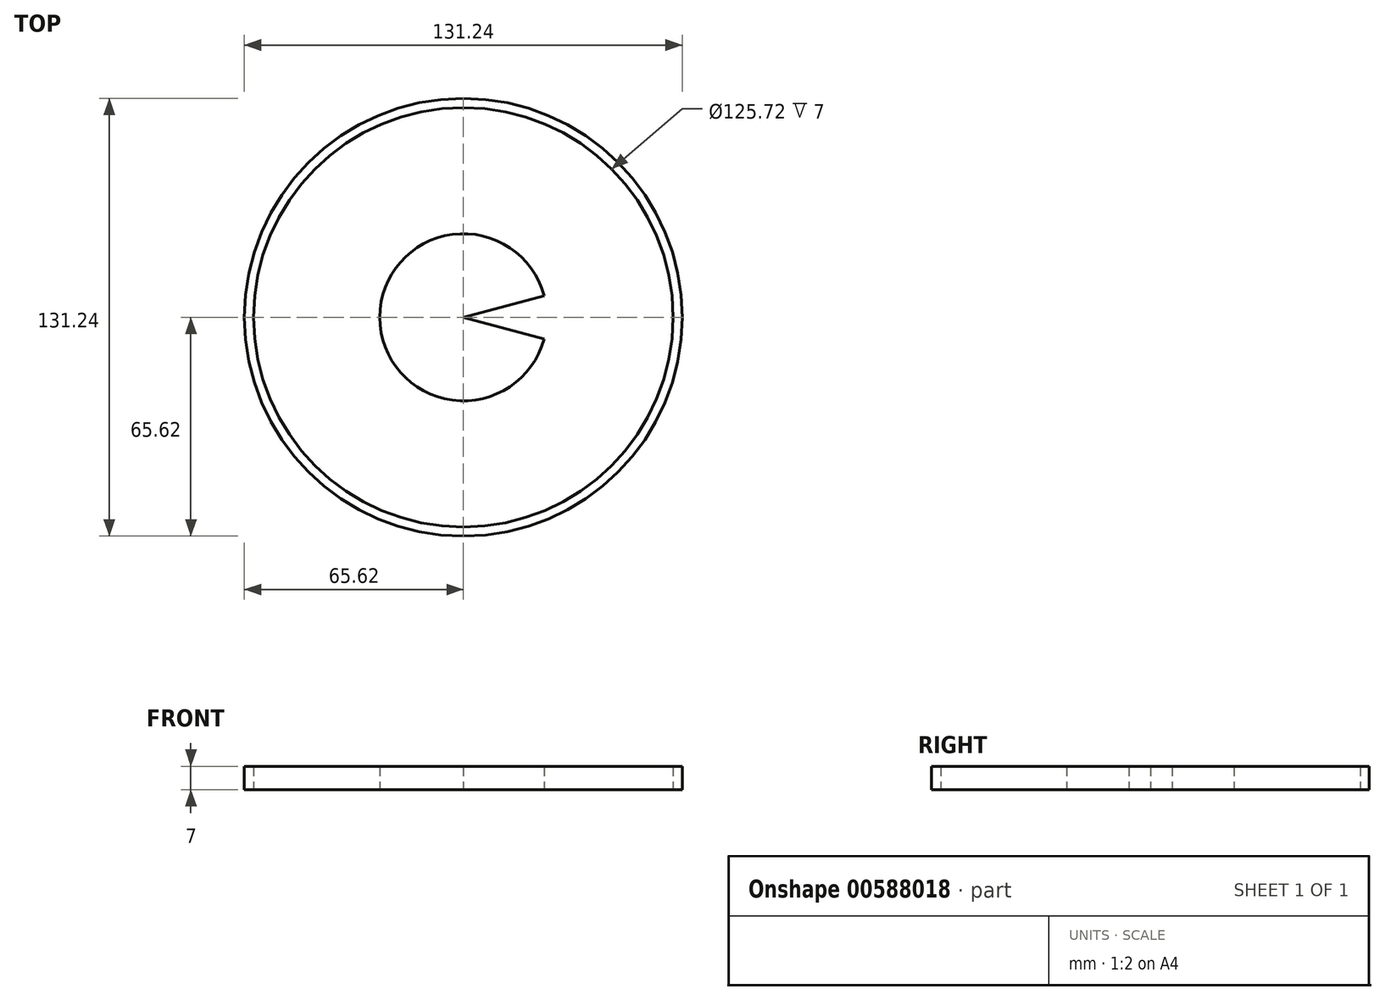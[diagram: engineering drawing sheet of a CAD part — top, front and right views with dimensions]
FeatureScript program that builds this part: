
annotation { "Feature Type Name" : "Feature", "Feature Type Description" : "" }
export const myFeature = defineFeature(function(context is Context, id is Id, definition is map)
    precondition{}
    {
        {
            var Q0;
            Q0=qCreatedBy(makeId("Top.planeOp"),FACE);
            var sketch = newSketch(context, id + "F0", { "sketchPlane" : qUnion([Q0])});
            skCircle(sketch, "E0", {"center": v(0, 0) * mm, "radius": 65.62 * mm});
            skCircle(sketch, "E1", {"center": v(0, 0) * mm, "radius": 62.86 * mm});
            skCircle(sketch, "E2.cCircle", {"center": v(0, 0) * mm, "radius": 65.62 * mm, "construction": true});
            skLineSegment(sketch, "E2.0", {"start": v(-17.58, 65.62) * mm, "end": v(17.58, 65.62) * mm});
            skLineSegment(sketch, "E2.1", {"start": v(17.58, 65.62) * mm, "end": v(48.03, 48.03) * mm});
            skLineSegment(sketch, "E2.2", {"start": v(48.03, 48.03) * mm, "end": v(65.62, 17.58) * mm});
            skLineSegment(sketch, "E2.3", {"start": v(65.62, 17.58) * mm, "end": v(65.62, -17.58) * mm});
            skLineSegment(sketch, "E2.4", {"start": v(65.62, -17.58) * mm, "end": v(48.03, -48.03) * mm});
            skLineSegment(sketch, "E2.5", {"start": v(48.03, -48.03) * mm, "end": v(17.58, -65.62) * mm});
            skLineSegment(sketch, "E2.6", {"start": v(17.58, -65.62) * mm, "end": v(-17.58, -65.62) * mm});
            skLineSegment(sketch, "E2.7", {"start": v(-17.58, -65.62) * mm, "end": v(-48.03, -48.03) * mm});
            skLineSegment(sketch, "E2.8", {"start": v(-48.03, -48.03) * mm, "end": v(-65.62, -17.58) * mm});
            skLineSegment(sketch, "E2.9", {"start": v(-65.62, -17.58) * mm, "end": v(-65.62, 17.58) * mm});
            skLineSegment(sketch, "E2.10", {"start": v(-65.62, 17.58) * mm, "end": v(-48.03, 48.03) * mm});
            skLineSegment(sketch, "E2.11", {"start": v(-48.03, 48.03) * mm, "end": v(-17.58, 65.62) * mm});
            skPoint(sketch, "E2.0.midPoint", {"position": v(0, 65.62) * mm});
            skCircle(sketch, "E3", {"center": v(0, 0) * mm, "radius": 25.05 * mm});
            skLineSegment(sketch, "E4", {"start": v(-17.58, 65.62) * mm, "end": v(17.58, -65.62) * mm});
            skLineSegment(sketch, "E5", {"start": v(17.58, 65.62) * mm, "end": v(-17.58, -65.62) * mm});
            skLineSegment(sketch, "E6", {"start": v(48.03, 48.03) * mm, "end": v(-48.03, -48.03) * mm});
            skLineSegment(sketch, "E7", {"start": v(65.62, 17.58) * mm, "end": v(-65.62, -17.58) * mm});
            skLineSegment(sketch, "E8", {"start": v(-65.62, 17.58) * mm, "end": v(65.62, -17.58) * mm});
            skLineSegment(sketch, "E9", {"start": v(-48.03, 48.03) * mm, "end": v(48.03, -48.03) * mm});
            skSolve(sketch);
        }
        {
            var Q0;
            {var subQ5=sQuery(id+"F0.wireOp",EDGE,"E0");var subQ7=makeQuery(id+"F0.imprint","INTERSECT",VERTEX,{"derivedFrom":[subQ5,sQuery(id+"F0.wireOp",EDGE,"E2.10")]});Q0=makeQuery(id+"F0.imprint","IMPRINT",FACE,{"disambiguationData":[TD([[makeQuery(id+"F0.imprint","IMPRINT",EDGE,{"disambiguationData":[TD([[subQ7,1.0]])],"derivedFrom":subQ5}),1.0]])]});}
            var Q1;
            {var subQ1=sQuery(id+"F0.wireOp",EDGE,"E0");var subQ5=makeQuery(id+"F0.imprint","INTERSECT",VERTEX,{"derivedFrom":[subQ1,sQuery(id+"F0.wireOp",EDGE,"E2.11")]});Q1=makeQuery(id+"F0.imprint","IMPRINT",FACE,{"disambiguationData":[TD([[makeQuery(id+"F0.imprint","IMPRINT",EDGE,{"disambiguationData":[TD([[subQ5,1.0]])],"derivedFrom":subQ1}),1.0]])]});}
            var Q2;
            {var subQ1=sQuery(id+"F0.wireOp",EDGE,"E0");var subQ8=makeQuery(id+"F0.imprint","INTERSECT",VERTEX,{"derivedFrom":[subQ1,sQuery(id+"F0.wireOp",EDGE,"E2.0")]});Q2=makeQuery(id+"F0.imprint","IMPRINT",FACE,{"disambiguationData":[TD([[makeQuery(id+"F0.imprint","IMPRINT",EDGE,{"disambiguationData":[TD([[subQ8,1.0]])],"derivedFrom":subQ1}),1.0]])]});}
            var Q3;
            {var subQ1=sQuery(id+"F0.wireOp",EDGE,"E0");var subQ5=makeQuery(id+"F0.imprint","INTERSECT",VERTEX,{"derivedFrom":[subQ1,sQuery(id+"F0.wireOp",EDGE,"E2.1")]});Q3=makeQuery(id+"F0.imprint","IMPRINT",FACE,{"disambiguationData":[TD([[makeQuery(id+"F0.imprint","IMPRINT",EDGE,{"disambiguationData":[TD([[subQ5,1.0]])],"derivedFrom":subQ1}),1.0]])]});}
            var Q4;
            {var subQ5=sQuery(id+"F0.wireOp",EDGE,"E0");var subQ7=makeQuery(id+"F0.imprint","INTERSECT",VERTEX,{"derivedFrom":[subQ5,sQuery(id+"F0.wireOp",EDGE,"E2.9")]});Q4=makeQuery(id+"F0.imprint","IMPRINT",FACE,{"disambiguationData":[TD([[makeQuery(id+"F0.imprint","IMPRINT",EDGE,{"disambiguationData":[TD([[subQ7,1.0]])],"derivedFrom":subQ5}),1.0]])]});}
            var Q5;
            {var subQ5=sQuery(id+"F0.wireOp",EDGE,"E0");var subQ7=makeQuery(id+"F0.imprint","INTERSECT",VERTEX,{"derivedFrom":[subQ5,sQuery(id+"F0.wireOp",EDGE,"E2.8")]});Q5=makeQuery(id+"F0.imprint","IMPRINT",FACE,{"disambiguationData":[TD([[makeQuery(id+"F0.imprint","IMPRINT",EDGE,{"disambiguationData":[TD([[subQ7,1.0]])],"derivedFrom":subQ5}),1.0]])]});}
            var Q6;
            {var subQ1=sQuery(id+"F0.wireOp",EDGE,"E0");var subQ7=makeQuery(id+"F0.imprint","INTERSECT",VERTEX,{"derivedFrom":[subQ1,sQuery(id+"F0.wireOp",EDGE,"E2.7")]});Q6=makeQuery(id+"F0.imprint","IMPRINT",FACE,{"disambiguationData":[TD([[makeQuery(id+"F0.imprint","IMPRINT",EDGE,{"disambiguationData":[TD([[subQ7,1.0]])],"derivedFrom":subQ1}),1.0]])]});}
            var Q7;
            {var subQ1=sQuery(id+"F0.wireOp",EDGE,"E0");var subQ5=makeQuery(id+"F0.imprint","INTERSECT",VERTEX,{"derivedFrom":[subQ1,sQuery(id+"F0.wireOp",EDGE,"E2.6")]});Q7=makeQuery(id+"F0.imprint","IMPRINT",FACE,{"disambiguationData":[TD([[makeQuery(id+"F0.imprint","IMPRINT",EDGE,{"disambiguationData":[TD([[subQ5,1.0]])],"derivedFrom":subQ1}),1.0]])]});}
            var Q8;
            {var subQ1=sQuery(id+"F0.wireOp",EDGE,"E0");var subQ7=makeQuery(id+"F0.imprint","INTERSECT",VERTEX,{"derivedFrom":[subQ1,sQuery(id+"F0.wireOp",EDGE,"E2.5")]});Q8=makeQuery(id+"F0.imprint","IMPRINT",FACE,{"disambiguationData":[TD([[makeQuery(id+"F0.imprint","IMPRINT",EDGE,{"disambiguationData":[TD([[subQ7,1.0]])],"derivedFrom":subQ1}),1.0]])]});}
            var Q9;
            {var subQ1=sQuery(id+"F0.wireOp",EDGE,"E0");var subQ5=makeQuery(id+"F0.imprint","INTERSECT",VERTEX,{"derivedFrom":[subQ1,sQuery(id+"F0.wireOp",EDGE,"E2.4")]});Q9=makeQuery(id+"F0.imprint","IMPRINT",FACE,{"disambiguationData":[TD([[makeQuery(id+"F0.imprint","IMPRINT",EDGE,{"disambiguationData":[TD([[subQ5,1.0]])],"derivedFrom":subQ1}),1.0]])]});}
            var Q10;
            {var subQ1=sQuery(id+"F0.wireOp",EDGE,"E0");var subQ5=makeQuery(id+"F0.imprint","INTERSECT",VERTEX,{"derivedFrom":[subQ1,sQuery(id+"F0.wireOp",EDGE,"E2.3")]});Q10=makeQuery(id+"F0.imprint","IMPRINT",FACE,{"disambiguationData":[TD([[makeQuery(id+"F0.imprint","IMPRINT",EDGE,{"disambiguationData":[TD([[subQ5,-1.0]])],"derivedFrom":subQ1}),1.0]])]});}
            var Q11;
            {var subQ1=sQuery(id+"F0.wireOp",EDGE,"E0");var subQ5=makeQuery(id+"F0.imprint","INTERSECT",VERTEX,{"derivedFrom":[subQ1,sQuery(id+"F0.wireOp",EDGE,"E2.2")]});Q11=makeQuery(id+"F0.imprint","IMPRINT",FACE,{"disambiguationData":[TD([[makeQuery(id+"F0.imprint","IMPRINT",EDGE,{"disambiguationData":[TD([[subQ5,1.0]])],"derivedFrom":subQ1}),1.0]])]});}
            var Q12;
            {var subQ0=sQuery(id+"F0.wireOp",EDGE,"E6");var subQ1=sQuery(id+"F0.wireOp",EDGE,"E3");var subQ2=makeQuery(id+"F0.imprint","INTERSECT",VERTEX,{"disambiguationData":[OD(0.0)],"derivedFrom":[subQ1,subQ0]});Q12=makeQuery(id+"F0.imprint","IMPRINT",FACE,{"disambiguationData":[TD([[makeQuery(id+"F0.imprint","IMPRINT",EDGE,{"disambiguationData":[TD([[subQ2,1.0]])],"derivedFrom":subQ1}),1.0]])]});}
            var Q13;
            {var subQ0=sQuery(id+"F0.wireOp",EDGE,"E5");var subQ1=sQuery(id+"F0.wireOp",EDGE,"E3");var subQ2=makeQuery(id+"F0.imprint","INTERSECT",VERTEX,{"disambiguationData":[OD(0.0)],"derivedFrom":[subQ1,subQ0]});Q13=makeQuery(id+"F0.imprint","IMPRINT",FACE,{"disambiguationData":[TD([[makeQuery(id+"F0.imprint","IMPRINT",EDGE,{"disambiguationData":[TD([[subQ2,-1.0]])],"derivedFrom":subQ1}),1.0]])]});}
            var Q14;
            {var subQ0=sQuery(id+"F0.wireOp",EDGE,"E7");var subQ1=sQuery(id+"F0.wireOp",EDGE,"E3");var subQ2=makeQuery(id+"F0.imprint","INTERSECT",VERTEX,{"disambiguationData":[OD(1.0)],"derivedFrom":[subQ1,subQ0]});Q14=makeQuery(id+"F0.imprint","IMPRINT",FACE,{"disambiguationData":[TD([[makeQuery(id+"F0.imprint","IMPRINT",EDGE,{"disambiguationData":[TD([[subQ2,-1.0]])],"derivedFrom":subQ1}),1.0]])]});}
            var Q15;
            {var subQ0=sQuery(id+"F0.wireOp",EDGE,"E6");var subQ1=sQuery(id+"F0.wireOp",EDGE,"E3");var subQ2=makeQuery(id+"F0.imprint","INTERSECT",VERTEX,{"disambiguationData":[OD(1.0)],"derivedFrom":[subQ1,subQ0]});Q15=makeQuery(id+"F0.imprint","IMPRINT",FACE,{"disambiguationData":[TD([[makeQuery(id+"F0.imprint","IMPRINT",EDGE,{"disambiguationData":[TD([[subQ2,-1.0]])],"derivedFrom":subQ1}),1.0]])]});}
            var Q16;
            {var subQ0=sQuery(id+"F0.wireOp",EDGE,"E5");var subQ1=sQuery(id+"F0.wireOp",EDGE,"E3");var subQ2=makeQuery(id+"F0.imprint","INTERSECT",VERTEX,{"disambiguationData":[OD(1.0)],"derivedFrom":[subQ1,subQ0]});Q16=makeQuery(id+"F0.imprint","IMPRINT",FACE,{"disambiguationData":[TD([[makeQuery(id+"F0.imprint","IMPRINT",EDGE,{"disambiguationData":[TD([[subQ2,-1.0]])],"derivedFrom":subQ1}),1.0]])]});}
            var Q17;
            {var subQ0=sQuery(id+"F0.wireOp",EDGE,"E4");var subQ1=sQuery(id+"F0.wireOp",EDGE,"E3");var subQ2=makeQuery(id+"F0.imprint","INTERSECT",VERTEX,{"disambiguationData":[OD(1.0)],"derivedFrom":[subQ1,subQ0]});Q17=makeQuery(id+"F0.imprint","IMPRINT",FACE,{"disambiguationData":[TD([[makeQuery(id+"F0.imprint","IMPRINT",EDGE,{"disambiguationData":[TD([[subQ2,-1.0]])],"derivedFrom":subQ1}),1.0]])]});}
            var Q18;
            {var subQ0=sQuery(id+"F0.wireOp",EDGE,"E9");var subQ1=sQuery(id+"F0.wireOp",EDGE,"E3");var subQ2=makeQuery(id+"F0.imprint","INTERSECT",VERTEX,{"disambiguationData":[OD(1.0)],"derivedFrom":[subQ1,subQ0]});Q18=makeQuery(id+"F0.imprint","IMPRINT",FACE,{"disambiguationData":[TD([[makeQuery(id+"F0.imprint","IMPRINT",EDGE,{"disambiguationData":[TD([[subQ2,-1.0]])],"derivedFrom":subQ1}),1.0]])]});}
            var Q19;
            {var subQ0=sQuery(id+"F0.wireOp",EDGE,"E7");var subQ1=sQuery(id+"F0.wireOp",EDGE,"E3");var subQ2=makeQuery(id+"F0.imprint","INTERSECT",VERTEX,{"disambiguationData":[OD(0.0)],"derivedFrom":[subQ1,subQ0]});Q19=makeQuery(id+"F0.imprint","IMPRINT",FACE,{"disambiguationData":[TD([[makeQuery(id+"F0.imprint","IMPRINT",EDGE,{"disambiguationData":[TD([[subQ2,1.0]])],"derivedFrom":subQ1}),1.0]])]});}
            var Q20;
            {var subQ0=sQuery(id+"F0.wireOp",EDGE,"E4");var subQ1=sQuery(id+"F0.wireOp",EDGE,"E3");var subQ2=makeQuery(id+"F0.imprint","INTERSECT",VERTEX,{"disambiguationData":[OD(0.0)],"derivedFrom":[subQ1,subQ0]});Q20=makeQuery(id+"F0.imprint","IMPRINT",FACE,{"disambiguationData":[TD([[makeQuery(id+"F0.imprint","IMPRINT",EDGE,{"disambiguationData":[TD([[subQ2,-1.0]])],"derivedFrom":subQ1}),1.0]])]});}
            var Q21;
            {var subQ0=sQuery(id+"F0.wireOp",EDGE,"E9");var subQ1=sQuery(id+"F0.wireOp",EDGE,"E3");var subQ2=makeQuery(id+"F0.imprint","INTERSECT",VERTEX,{"disambiguationData":[OD(0.0)],"derivedFrom":[subQ1,subQ0]});Q21=makeQuery(id+"F0.imprint","IMPRINT",FACE,{"disambiguationData":[TD([[makeQuery(id+"F0.imprint","IMPRINT",EDGE,{"disambiguationData":[TD([[subQ2,-1.0]])],"derivedFrom":subQ1}),1.0]])]});}
            var Q22;
            {var subQ0=sQuery(id+"F0.wireOp",EDGE,"E8");var subQ1=sQuery(id+"F0.wireOp",EDGE,"E3");var subQ2=makeQuery(id+"F0.imprint","INTERSECT",VERTEX,{"disambiguationData":[OD(0.0)],"derivedFrom":[subQ1,subQ0]});Q22=makeQuery(id+"F0.imprint","IMPRINT",FACE,{"disambiguationData":[TD([[makeQuery(id+"F0.imprint","IMPRINT",EDGE,{"disambiguationData":[TD([[subQ2,-1.0]])],"derivedFrom":subQ1}),1.0]])]});}
            var Q23;
            {var subQ0=sQuery(id+"F0.wireOp",EDGE,"E6");var subQ1=sQuery(id+"F0.wireOp",EDGE,"E3");var subQ2=makeQuery(id+"F0.imprint","INTERSECT",VERTEX,{"disambiguationData":[OD(0.0)],"derivedFrom":[subQ1,subQ0]});Q23=makeQuery(id+"F0.imprint","IMPRINT",FACE,{"disambiguationData":[TD([[makeQuery(id+"F0.imprint","IMPRINT",EDGE,{"disambiguationData":[TD([[subQ2,-1.0]])],"derivedFrom":subQ1}),1.0]])]});}
            extrude(context, id + "F1", {"entities" : qUnion([Q0, Q1, Q2, Q3, Q4, Q5, Q6, Q7, Q8, Q9, Q10, Q11, Q12, Q13, Q14, Q15, Q16, Q17, Q18, Q19, Q20, Q21, Q22, Q23]), "depth" : 7 * mm, "offsetDistance" : 25 * mm});
        }
        {
            var Q0;
            Q0=sQuery(id+"F0.wireOp",EDGE,"E3");
            extrude(context, id + "F2", {"bodyType" : ToolBodyType.SURFACE, "surfaceEntities" : qUnion([Q0]), "oppositeDirection" : true, "depth" : 25 * mm, "offsetDistance" : 25 * mm});
        }
    });
